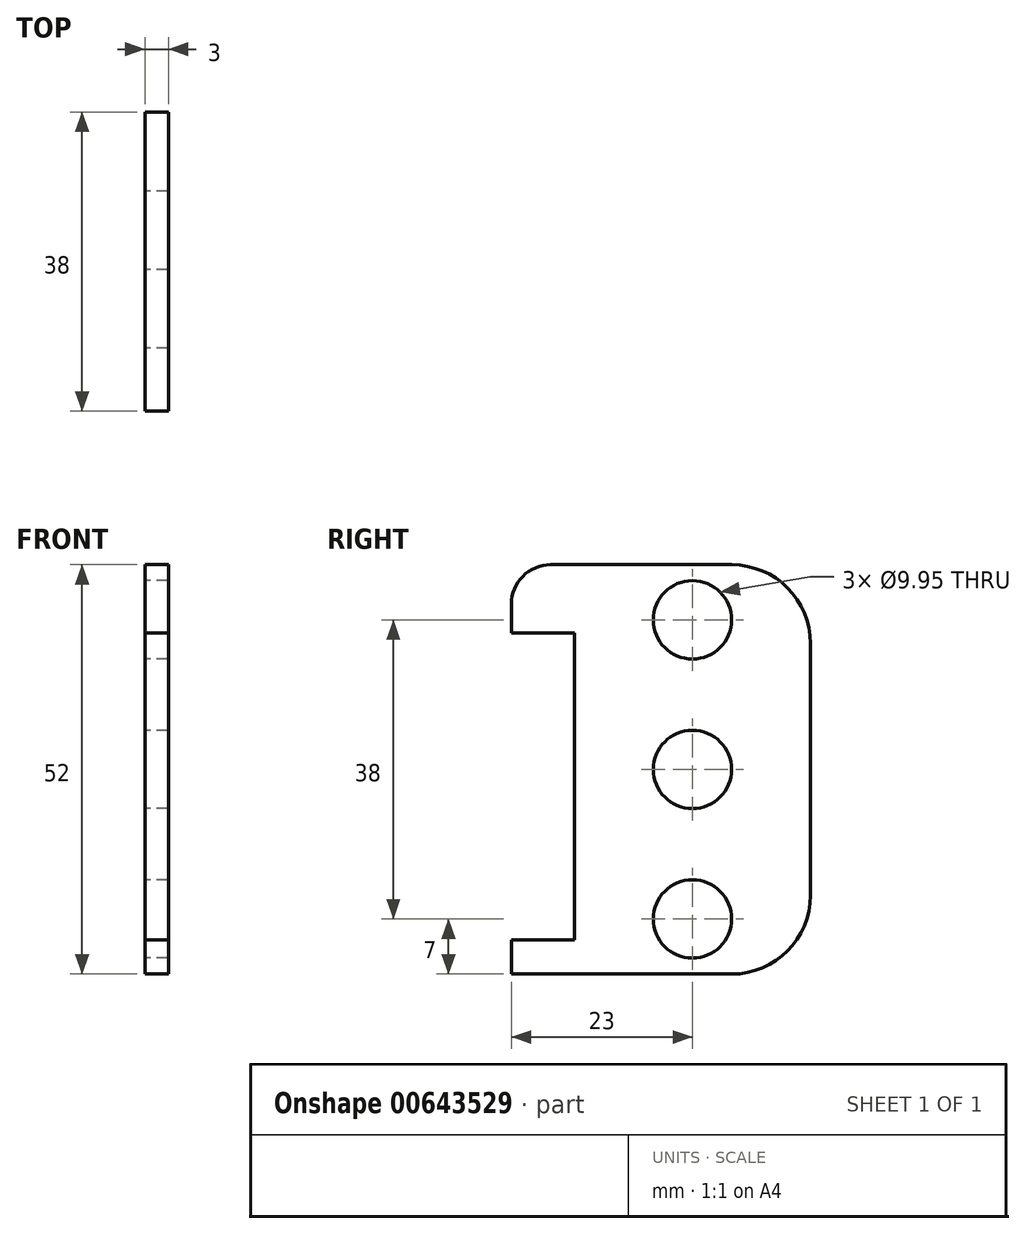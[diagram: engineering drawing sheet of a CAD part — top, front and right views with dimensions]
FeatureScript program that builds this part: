
annotation { "Feature Type Name" : "Feature", "Feature Type Description" : "" }
export const myFeature = defineFeature(function(context is Context, id is Id, definition is map)
    precondition{}
    {
        {
            var Q0;
            Q0=qCreatedBy(makeId("Right.planeOp"),FACE);
            var sketch = newSketch(context, id + "F0", { "sketchPlane" : qUnion([Q0])});
            skLineSegment(sketch, "E0.bottom", {"start": v(19, 26) * mm, "end": v(-19, 26) * mm, "construction": true});
            skLineSegment(sketch, "E0.top", {"start": v(19, -26) * mm, "end": v(-19, -26) * mm, "construction": true});
            skLineSegment(sketch, "E0.left", {"start": v(19, 26) * mm, "end": v(19, -26) * mm, "construction": true});
            skLineSegment(sketch, "E0.right", {"start": v(-19, 26) * mm, "end": v(-19, -26) * mm, "construction": true});
            skPoint(sketch, "E0.middle", {"position": v(0, 0) * mm});
            skLineSegment(sketch, "E1", {"start": v(-19, 21) * mm, "end": v(-19, 17.3) * mm});
            skLineSegment(sketch, "E2", {"start": v(-19, 17.3) * mm, "end": v(-11, 17.3) * mm});
            skLineSegment(sketch, "E3", {"start": v(-11, 17.3) * mm, "end": v(-11, -21.65) * mm});
            skLineSegment(sketch, "E4", {"start": v(-11, -21.65) * mm, "end": v(-19, -21.65) * mm});
            skLineSegment(sketch, "E5", {"start": v(-19, -21.65) * mm, "end": v(-19, -26) * mm});
            skLineSegment(sketch, "E6", {"start": v(19, -16) * mm, "end": v(19, 16) * mm});
            skLineSegment(sketch, "E7", {"start": v(9, 26) * mm, "end": v(-14, 26) * mm});
            skLineSegment(sketch, "E8", {"start": v(-19, -26) * mm, "end": v(9, -26) * mm});
            skPoint(sketch, "E9.visualSharp", {"position": v(19, 26) * mm});
            skArc(sketch, "E9.filletArc", {"start": v(19, 16) * mm, "mid": v(16.07, 23.07) * mm, "end": v(9, 26) * mm});
            skPoint(sketch, "E10.visualSharp", {"position": v(19, -26) * mm});
            skArc(sketch, "E10.filletArc", {"start": v(9, -26) * mm, "mid": v(16.07, -23.07) * mm, "end": v(19, -16) * mm});
            skCircle(sketch, "E11", {"center": v(4, 19) * mm, "radius": 2.65 * mm, "construction": true});
            skCircle(sketch, "E12", {"center": v(4, -19) * mm, "radius": 2.65 * mm, "construction": true});
            skLineSegment(sketch, "E13", {"start": v(4, -19) * mm, "end": v(4, 19) * mm, "construction": true});
            skCircle(sketch, "E14", {"center": v(4, 0) * mm, "radius": 4.25 * mm, "construction": true});
            skCircle(sketch, "E15", {"center": v(4, 19) * mm, "radius": 4.97 * mm});
            skCircle(sketch, "E16", {"center": v(4, -19) * mm, "radius": 4.97 * mm});
            skCircle(sketch, "E17", {"center": v(4, 0) * mm, "radius": 4.97 * mm});
            skCircle(sketch, "E18", {"center": v(4, 0) * mm, "radius": 10.97 * mm, "construction": true});
            skPoint(sketch, "E19.visualSharp", {"position": v(-19, 26) * mm});
            skArc(sketch, "E19.filletArc", {"start": v(-14, 26) * mm, "mid": v(-17.54, 24.54) * mm, "end": v(-19, 21) * mm});
            skSolve(sketch);
        }
        {
            var Q0;
            Q0=qSketchRegion(id+"F0",true);
            extrude(context, id + "F1", {"entities" : qUnion([Q0]), "depth" : 3 * mm, "offsetDistance" : 25 * mm});
        }
    });
